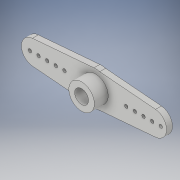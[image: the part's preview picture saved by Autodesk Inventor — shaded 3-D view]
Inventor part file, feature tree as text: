
AUTODESK INVENTOR PART (.ipt)
format: ipt  version: 2017 (Build 210142000, 142)  size: 143,360 bytes
history: native  units: in
note: dims shown in document units (in); Inventor stores cm internally (conversion verified against a paired STEP export)
features: extrude x4, sketch x4
ambient origin geometry x8: Origin, YZ Plane, XZ Plane, XY Plane, X Axis, Y Axis, Z Axis, Center Point
bodies: Body1 (feature_tree)
feature tree (8):
  extrude  "Extrusion2"  Depth=0.35in
  extrude  "Extrusion3"  Depth=0.085in TaperAngle=0.0deg
  extrude  "Extrusion4"  Depth=0.2in TaperAngle=0.0deg
  extrude  "Extrusion5"  Depth=0.2in TaperAngle=0.0deg
  sketch  "Sketch2"  dims[d4=0.5in d5=0.35in]
  sketch  "Sketch3"  dims[d6=0.35in d9=0.085in d10=0.0in]
  sketch  "Sketch4"  dims[d11=0.37in d12=0.2in d13=0.0in]
  sketch  "Sketch5"  dims[d14=0.2in d15=0.2in d16=0.0in d17=0.05in d18=0.1in d19=1.9685in d21=0.125in d22=0.3937in d24=1.0in d26=0.2in d27=0.0in]
